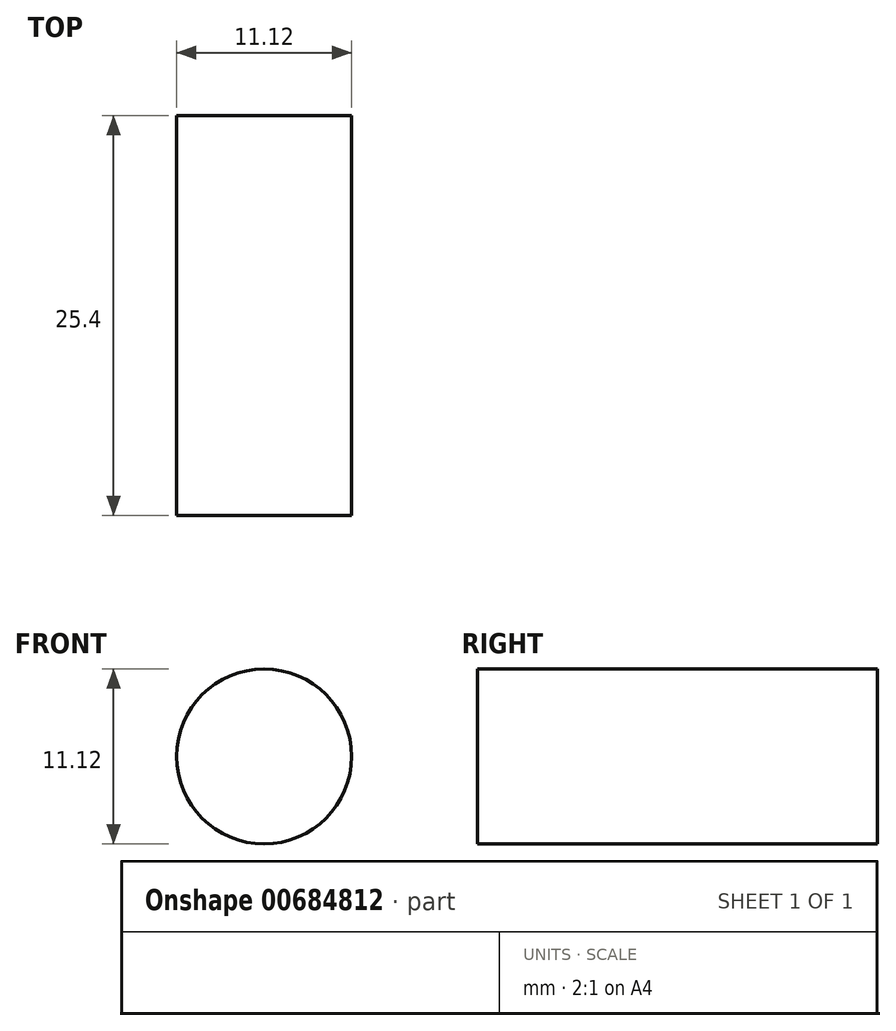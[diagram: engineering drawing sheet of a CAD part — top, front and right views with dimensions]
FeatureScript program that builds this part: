
annotation { "Feature Type Name" : "Feature", "Feature Type Description" : "" }
export const myFeature = defineFeature(function(context is Context, id is Id, definition is map)
    precondition{}
    {
        {
            var Q0;
            Q0=qCreatedBy(makeId("Front.planeOp"),FACE);
            var sketch = newSketch(context, id + "F0", { "sketchPlane" : qUnion([Q0])});
            skCircle(sketch, "E0", {"center": v(0, 0) * mm, "radius": 5.56 * mm});
            skSolve(sketch);
        }
        {
            var Q0;
            Q0=makeQuery(id+"F0.imprint","IMPRINT",FACE,{"disambiguationData":[TD([[makeQuery(id+"F0.imprint","IMPRINT",EDGE,{"derivedFrom":sQuery(id+"F0.wireOp",EDGE,"E0")}),1.0]])]});
            extrude(context, id + "F1", {"entities" : qUnion([Q0]), "depth" : 25.4 * mm, "offsetDistance" : 25.4 * mm});
        }
    });
